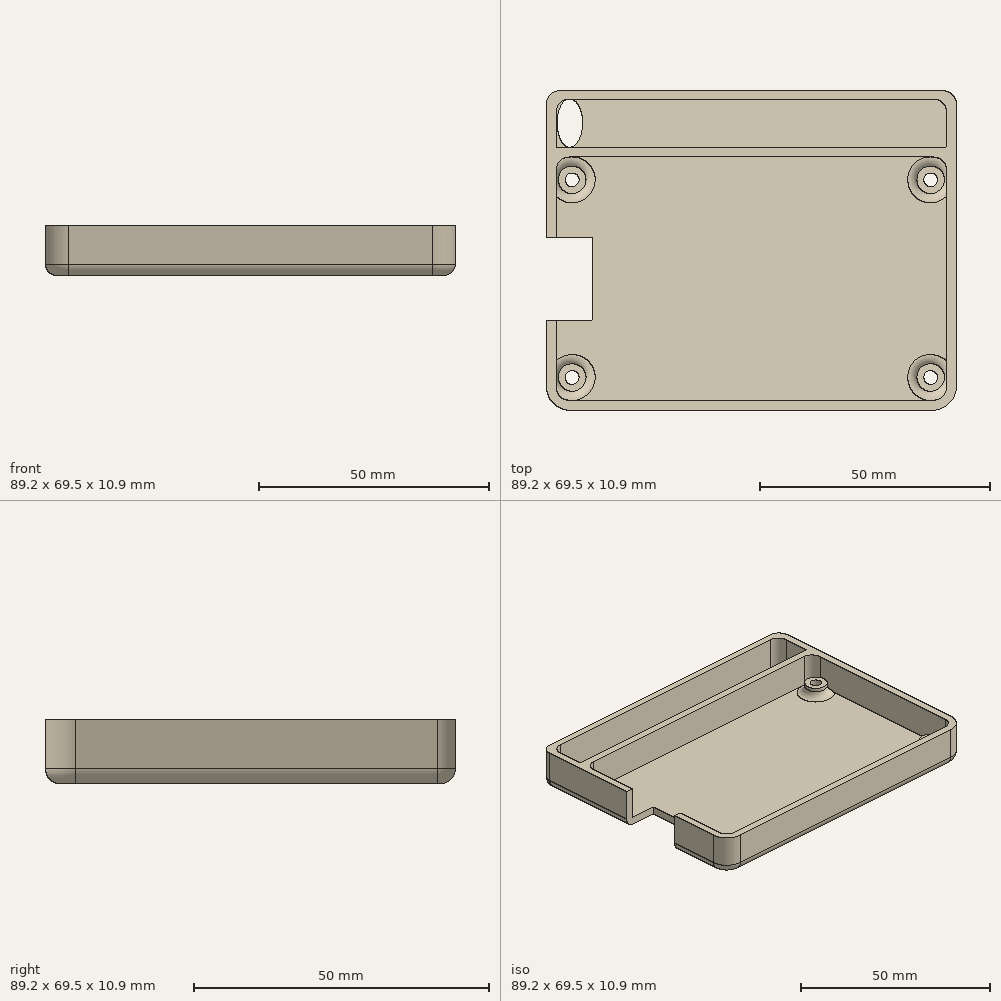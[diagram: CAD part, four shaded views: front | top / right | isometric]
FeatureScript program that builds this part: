
annotation { "Feature Type Name" : "Feature", "Feature Type Description" : "" }
export const myFeature = defineFeature(function(context is Context, id is Id, definition is map)
    precondition{}
    {
        {
            var Q0;
            Q0=qCreatedBy(makeId("Top.planeOp"),FACE);
            var sketch = newSketch(context, id + "F0", { "sketchPlane" : qUnion([Q0])});
            skLineSegment(sketch, "E0.bottom", {"start": v(-39.5, 26.5) * mm, "end": v(39.5, 26.5) * mm});
            skLineSegment(sketch, "E0.top", {"start": v(-39.5, -26.5) * mm, "end": v(39.5, -26.5) * mm});
            skLineSegment(sketch, "E0.left", {"start": v(-42.5, 23.5) * mm, "end": v(-42.5, -23.5) * mm});
            skLineSegment(sketch, "E0.right", {"start": v(42.5, 23.5) * mm, "end": v(42.5, -23.5) * mm});
            skPoint(sketch, "E0.middle", {"position": v(0, 0) * mm});
            skLineSegment(sketch, "E1.bottom", {"start": v(-39, 21.5) * mm, "end": v(39, 21.5) * mm, "construction": true});
            skLineSegment(sketch, "E1.top", {"start": v(-39, -21.5) * mm, "end": v(39, -21.5) * mm, "construction": true});
            skLineSegment(sketch, "E1.left", {"start": v(-39, 21.5) * mm, "end": v(-39, -21.5) * mm, "construction": true});
            skLineSegment(sketch, "E1.right", {"start": v(39, 21.5) * mm, "end": v(39, -21.5) * mm, "construction": true});
            skCircle(sketch, "E2", {"center": v(-39, 21.5) * mm, "radius": 1.5 * mm});
            skCircle(sketch, "E3", {"center": v(39, 21.5) * mm, "radius": 1.5 * mm});
            skCircle(sketch, "E4", {"center": v(39, -21.5) * mm, "radius": 1.5 * mm});
            skCircle(sketch, "E5", {"center": v(-39, -21.5) * mm, "radius": 1.5 * mm});
            skPoint(sketch, "E6.visualSharp", {"position": v(-42.5, 26.5) * mm});
            skArc(sketch, "E6.filletArc", {"start": v(-39.5, 26.5) * mm, "mid": v(-41.62, 25.62) * mm, "end": v(-42.5, 23.5) * mm});
            skPoint(sketch, "E7.visualSharp", {"position": v(42.5, 26.5) * mm});
            skArc(sketch, "E7.filletArc", {"start": v(42.5, 23.5) * mm, "mid": v(41.62, 25.62) * mm, "end": v(39.5, 26.5) * mm});
            skPoint(sketch, "E8.visualSharp", {"position": v(42.5, -26.5) * mm});
            skArc(sketch, "E8.filletArc", {"start": v(39.5, -26.5) * mm, "mid": v(41.62, -25.62) * mm, "end": v(42.5, -23.5) * mm});
            skPoint(sketch, "E9.visualSharp", {"position": v(-42.5, -26.5) * mm});
            skArc(sketch, "E9.filletArc", {"start": v(-42.5, -23.5) * mm, "mid": v(-41.62, -25.62) * mm, "end": v(-39.5, -26.5) * mm});
            skLineSegment(sketch, "E10", {"start": v(0, 0) * mm, "end": v(-34.5, 0) * mm, "construction": true});
            skLineSegment(sketch, "E11", {"start": v(-34.5, 26.5) * mm, "end": v(-34.5, -26.5) * mm});
            skLineSegment(sketch, "E12", {"start": v(0, 0) * mm, "end": v(0, 9.32) * mm, "construction": true});
            skLineSegment(sketch, "E13.MirrorCS", {"start": v(34.5, 26.5) * mm, "end": v(34.5, -26.5) * mm});
            skLineSegment(sketch, "E14.1", {"start": v(-44.6, 23.5) * mm, "end": v(-44.6, -23.5) * mm});
            skLineSegment(sketch, "E14.2", {"start": v(-39.5, 28.6) * mm, "end": v(39.5, 28.6) * mm});
            skArc(sketch, "E14.3", {"start": v(-44.6, -23.5) * mm, "mid": v(-43.1, -27.1) * mm, "end": v(-39.5, -28.6) * mm});
            skLineSegment(sketch, "E14.5", {"start": v(44.6, 23.5) * mm, "end": v(44.6, -23.5) * mm});
            skArc(sketch, "E14.6", {"start": v(39.5, -28.6) * mm, "mid": v(43.1, -27.1) * mm, "end": v(44.6, -23.5) * mm});
            skLineSegment(sketch, "E14.7", {"start": v(-39.5, -28.6) * mm, "end": v(39.5, -28.6) * mm});
            skLineSegment(sketch, "E15", {"start": v(-42.5, 0) * mm, "end": v(-44.6, 0) * mm, "construction": true});
            skLineSegment(sketch, "E16.bottom", {"start": v(-44.6, 9) * mm, "end": v(-42.5, 9) * mm});
            skLineSegment(sketch, "E16.top", {"start": v(-44.6, -9) * mm, "end": v(-42.5, -9) * mm});
            skLineSegment(sketch, "E16.left", {"start": v(-44.6, 9) * mm, "end": v(-44.6, -9) * mm});
            skLineSegment(sketch, "E16.right", {"start": v(-42.5, 9) * mm, "end": v(-42.5, -9) * mm});
            skPoint(sketch, "E16.middle", {"position": v(-43.55, 0) * mm});
            skLineSegment(sketch, "E17", {"start": v(-42.5, 9) * mm, "end": v(-34.5, 9) * mm});
            skLineSegment(sketch, "E18", {"start": v(-42.5, -9) * mm, "end": v(-34.5, -9) * mm});
            skLineSegment(sketch, "E19", {"start": v(0, 28.6) * mm, "end": v(0, 39.1) * mm, "construction": true});
            skLineSegment(sketch, "E20", {"start": v(0, 39.1) * mm, "end": v(-39.5, 39.1) * mm});
            skLineSegment(sketch, "E21", {"start": v(0, 39.1) * mm, "end": v(39.5, 39.1) * mm});
            skLineSegment(sketch, "E22.0", {"start": v(0, 40.9) * mm, "end": v(41.6, 40.9) * mm});
            skLineSegment(sketch, "E22.1", {"start": v(0, 40.9) * mm, "end": v(-41.6, 40.9) * mm});
            skLineSegment(sketch, "E23", {"start": v(-42.5, 23.5) * mm, "end": v(-42.5, 36.1) * mm});
            skLineSegment(sketch, "E24", {"start": v(42.5, 23.5) * mm, "end": v(42.5, 36.1) * mm});
            skPoint(sketch, "E25.visualSharp", {"position": v(42.5, 39.1) * mm});
            skArc(sketch, "E25.filletArc", {"start": v(42.5, 36.1) * mm, "mid": v(41.62, 38.22) * mm, "end": v(39.5, 39.1) * mm});
            skPoint(sketch, "E26.visualSharp", {"position": v(-42.5, 39.1) * mm});
            skArc(sketch, "E26.filletArc", {"start": v(-39.5, 39.1) * mm, "mid": v(-41.62, 38.22) * mm, "end": v(-42.5, 36.1) * mm});
            skPoint(sketch, "E27.start.orphan", {"position": v(-44.6, 39.1) * mm});
            skPoint(sketch, "E28.start.orphan", {"position": v(44.6, 39.1) * mm});
            skLineSegment(sketch, "E29", {"start": v(-44.6, 23.5) * mm, "end": v(-44.6, 37.9) * mm});
            skLineSegment(sketch, "E30", {"start": v(44.6, 23.5) * mm, "end": v(44.6, 37.9) * mm});
            skPoint(sketch, "E31.visualSharp", {"position": v(-44.6, 40.9) * mm});
            skArc(sketch, "E31.filletArc", {"start": v(-41.6, 40.9) * mm, "mid": v(-43.72, 40.02) * mm, "end": v(-44.6, 37.9) * mm});
            skPoint(sketch, "E32.visualSharp", {"position": v(44.6, 40.9) * mm});
            skArc(sketch, "E32.filletArc", {"start": v(44.6, 37.9) * mm, "mid": v(43.72, 40.02) * mm, "end": v(41.6, 40.9) * mm});
            skLineSegment(sketch, "E33", {"start": v(-39.5, 28.6) * mm, "end": v(-42.5, 28.6) * mm});
            skLineSegment(sketch, "E34", {"start": v(39.5, 28.6) * mm, "end": v(42.5, 28.6) * mm});
            skEllipse(sketch, "E35", {"center": v(-39.5, 33.85) * mm, "majorRadius": 5.25 * mm, "minorRadius": 2.78 * mm, "majorAxis": v(0, 1)});
            skPoint(sketch, "E35.centerSnap0", {"position": v(0, 33.85) * mm});
            skCircle(sketch, "E36", {"center": v(-39, 21.5) * mm, "radius": 3 * mm});
            skCircle(sketch, "E37", {"center": v(39, 21.5) * mm, "radius": 3 * mm});
            skCircle(sketch, "E38", {"center": v(39, -21.5) * mm, "radius": 3 * mm});
            skCircle(sketch, "E39", {"center": v(-39, -21.5) * mm, "radius": 3 * mm});
            skSolve(sketch);
        }
        {
            var Q0;
            {var subQ13=sQuery(id+"F0.wireOp",EDGE,"E0.right");Q0=makeQuery(id+"F0.imprint","IMPRINT",FACE,{"disambiguationData":[TD([[makeQuery(id+"F0.imprint","IMPRINT",EDGE,{"derivedFrom":subQ13}),1.0]])]});}
            var Q1;
            Q1=makeQuery(id+"F0.imprint","IMPRINT",FACE,{"disambiguationData":[TD([[makeQuery(id+"F0.imprint","IMPRINT",EDGE,{"derivedFrom":sQuery(id+"F0.wireOp",EDGE,"E2")}),-1.0]])]});
            var Q2;
            Q2=makeQuery(id+"F0.imprint","IMPRINT",FACE,{"disambiguationData":[TD([[makeQuery(id+"F0.imprint","IMPRINT",EDGE,{"derivedFrom":sQuery(id+"F0.wireOp",EDGE,"E5")}),-1.0]])]});
            var Q3;
            {var subQ5=sQuery(id+"F0.wireOp",EDGE,"E13.MirrorCS");Q3=makeQuery(id+"F0.imprint","IMPRINT",FACE,{"disambiguationData":[TD([[makeQuery(id+"F0.imprint","IMPRINT",EDGE,{"derivedFrom":subQ5}),-1.0]])]});}
            var Q4;
            Q4=makeQuery(id+"F0.imprint","IMPRINT",FACE,{"disambiguationData":[TD([[makeQuery(id+"F0.imprint","IMPRINT",EDGE,{"derivedFrom":sQuery(id+"F0.wireOp",EDGE,"E0.right")}),-1.0]])]});
            var Q5;
            {var subQ0=sQuery(id+"F0.wireOp",EDGE,"E6.filletArc");Q5=makeQuery(id+"F0.imprint","IMPRINT",FACE,{"disambiguationData":[TD([[makeQuery(id+"F0.imprint","IMPRINT",EDGE,{"derivedFrom":subQ0}),-1.0]])]});}
            var Q6;
            {var subQ5=sQuery(id+"F0.wireOp",EDGE,"E14.2");Q6=makeQuery(id+"F0.imprint","IMPRINT",FACE,{"disambiguationData":[TD([[makeQuery(id+"F0.imprint","IMPRINT",EDGE,{"derivedFrom":subQ5}),1.0]])]});}
            var Q7;
            {var subQ0=sQuery(id+"F0.wireOp",EDGE,"E6.filletArc");Q7=makeQuery(id+"F0.imprint","IMPRINT",FACE,{"disambiguationData":[TD([[makeQuery(id+"F0.imprint","IMPRINT",EDGE,{"derivedFrom":subQ0}),-1.0]])]});}
            var Q8;
            {var subQ2=sQuery(id+"F0.wireOp",EDGE,"E26.filletArc");Q8=makeQuery(id+"F0.imprint","IMPRINT",FACE,{"disambiguationData":[TD([[makeQuery(id+"F0.imprint","IMPRINT",EDGE,{"derivedFrom":subQ2}),1.0]])]});}
            var Q9;
            {var subQ4=sQuery(id+"F0.wireOp",EDGE,"E6.filletArc");Q9=makeQuery(id+"F0.imprint","IMPRINT",FACE,{"disambiguationData":[TD([[makeQuery(id+"F0.imprint","IMPRINT",EDGE,{"derivedFrom":subQ4}),1.0]])]});}
            var Q10;
            {var subQ4=sQuery(id+"F0.wireOp",EDGE,"E9.filletArc");Q10=makeQuery(id+"F0.imprint","IMPRINT",FACE,{"disambiguationData":[TD([[makeQuery(id+"F0.imprint","IMPRINT",EDGE,{"derivedFrom":subQ4}),1.0]])]});}
            var Q11;
            Q11=makeQuery(id+"F0.imprint","IMPRINT",FACE,{"disambiguationData":[TD([[makeQuery(id+"F0.imprint","IMPRINT",EDGE,{"derivedFrom":sQuery(id+"F0.wireOp",EDGE,"E3")}),-1.0]])]});
            var Q12;
            Q12=makeQuery(id+"F0.imprint","IMPRINT",FACE,{"disambiguationData":[TD([[makeQuery(id+"F0.imprint","IMPRINT",EDGE,{"derivedFrom":sQuery(id+"F0.wireOp",EDGE,"E4")}),-1.0]])]});
            extrude(context, id + "F1", {"entities" : qUnion([Q0, Q1, Q2, Q3, Q4, Q5, Q6, Q7, Q8, Q9, Q10, Q11, Q12]), "depth" : 2.1 * mm, "offsetDistance" : 25 * mm});
        }
        {
            var Q0;
            {var subQ13=sQuery(id+"F0.wireOp",EDGE,"E0.right");Q0=makeQuery(id+"F0.imprint","IMPRINT",FACE,{"disambiguationData":[TD([[makeQuery(id+"F0.imprint","IMPRINT",EDGE,{"derivedFrom":subQ13}),1.0]])]});}
            var Q1;
            {var subQ0=sQuery(id+"F0.wireOp",EDGE,"E6.filletArc");Q1=makeQuery(id+"F0.imprint","IMPRINT",FACE,{"disambiguationData":[TD([[makeQuery(id+"F0.imprint","IMPRINT",EDGE,{"derivedFrom":subQ0}),-1.0]])]});}
            extrude(context, id + "F2", {"entities" : qUnion([Q0, Q1]), "operationType" : NewBodyOperationType.ADD, "depth" : (5.1 + 5.8) * mm, "offsetDistance" : 25 * mm});
        }
        {
            var Q0;
            Q0=makeQuery(id+"F1.opExtrude","CAP_EDGE",EDGE,{"disambiguationData":[OSD([sQuery(id+"F0.wireOp",EDGE,"E14.5"),sQuery(id+"F0.wireOp",EDGE,"E30")])],"isStart":true});
            fillet(context, id + "F3", {"entities" : qUnion([Q0]), "radius" : 2.5 * mm, "tangentPropagation" : true, "allowEdgeOverflow" : false});
        }
        {
            var Q0;
            Q0=makeQuery(id+"F0.imprint","IMPRINT",FACE,{"disambiguationData":[TD([[makeQuery(id+"F0.imprint","IMPRINT",EDGE,{"derivedFrom":sQuery(id+"F0.wireOp",EDGE,"E2")}),-1.0]])]});
            var Q1;
            Q1=makeQuery(id+"F0.imprint","IMPRINT",FACE,{"disambiguationData":[TD([[makeQuery(id+"F0.imprint","IMPRINT",EDGE,{"derivedFrom":sQuery(id+"F0.wireOp",EDGE,"E3")}),-1.0]])]});
            var Q2;
            Q2=makeQuery(id+"F0.imprint","IMPRINT",FACE,{"disambiguationData":[TD([[makeQuery(id+"F0.imprint","IMPRINT",EDGE,{"derivedFrom":sQuery(id+"F0.wireOp",EDGE,"E4")}),-1.0]])]});
            var Q3;
            Q3=makeQuery(id+"F0.imprint","IMPRINT",FACE,{"disambiguationData":[TD([[makeQuery(id+"F0.imprint","IMPRINT",EDGE,{"derivedFrom":sQuery(id+"F0.wireOp",EDGE,"E5")}),-1.0]])]});
            extrude(context, id + "F4", {"entities" : qUnion([Q0, Q1, Q2, Q3]), "operationType" : NewBodyOperationType.ADD, "depth" : 5.1 * mm, "offsetDistance" : 25 * mm});
        }
        {
            var Q0;
            {var subQ2=sQuery(id+"F0.wireOp",EDGE,"E18");var subQ3=sQuery(id+"F0.wireOp",EDGE,"E16.top");var subQ4=sQuery(id+"F0.wireOp",EDGE,"E17");var subQ5=sQuery(id+"F0.wireOp",EDGE,"E16.bottom");var subQ6=sQuery(id+"F0.wireOp",EDGE,"E11");var subQ7=sQuery(id+"F0.wireOp",EDGE,"E2");var subQ8=sQuery(id+"F0.wireOp",EDGE,"E5");var subQ10=sQuery(id+"F0.wireOp",EDGE,"E3");var subQ11=sQuery(id+"F0.wireOp",EDGE,"E4");Q0=makeQuery(id+"F4.boolean.opBoolean","INTERSECT",EDGE,{"derivedFrom":[makeQuery(id+"F2.boolean.opBoolean","SPLIT",FACE,{"disambiguationData":[TD([makeQuery(id+"F1.opExtrude","SWEPT_FACE",FACE,{"disambiguationData":[OSD([subQ7])]})])],"derivedFrom":makeQuery(id+"F1.opExtrude","CAP_FACE",FACE,{"disambiguationData":[OSD([subQ7,subQ10,subQ11,subQ8,subQ6,sQuery(id+"F0.wireOp",EDGE,"E14.1"),sQuery(id+"F0.wireOp",EDGE,"E14.3"),sQuery(id+"F0.wireOp",EDGE,"E14.5"),sQuery(id+"F0.wireOp",EDGE,"E14.6"),sQuery(id+"F0.wireOp",EDGE,"E14.7"),subQ5,subQ3,subQ4,subQ2,sQuery(id+"F0.wireOp",EDGE,"E22.0"),sQuery(id+"F0.wireOp",EDGE,"E22.1"),sQuery(id+"F0.wireOp",EDGE,"E29"),sQuery(id+"F0.wireOp",EDGE,"E30"),sQuery(id+"F0.wireOp",EDGE,"E31.filletArc"),sQuery(id+"F0.wireOp",EDGE,"E32.filletArc"),sQuery(id+"F0.wireOp",EDGE,"E35")])],"isStart":false})}),makeQuery(id+"F4.opExtrude","SWEPT_FACE",FACE,{"disambiguationData":[OSD([sQuery(id+"F0.wireOp",EDGE,"E36")])]})]});}
            var Q1;
            {var subQ2=sQuery(id+"F0.wireOp",EDGE,"E18");var subQ3=sQuery(id+"F0.wireOp",EDGE,"E16.top");var subQ4=sQuery(id+"F0.wireOp",EDGE,"E17");var subQ5=sQuery(id+"F0.wireOp",EDGE,"E16.bottom");var subQ6=sQuery(id+"F0.wireOp",EDGE,"E11");var subQ7=sQuery(id+"F0.wireOp",EDGE,"E2");var subQ8=sQuery(id+"F0.wireOp",EDGE,"E5");var subQ10=sQuery(id+"F0.wireOp",EDGE,"E3");var subQ11=sQuery(id+"F0.wireOp",EDGE,"E4");Q1=makeQuery(id+"F4.boolean.opBoolean","INTERSECT",EDGE,{"derivedFrom":[makeQuery(id+"F2.boolean.opBoolean","SPLIT",FACE,{"disambiguationData":[TD([makeQuery(id+"F1.opExtrude","SWEPT_FACE",FACE,{"disambiguationData":[OSD([subQ7])]})])],"derivedFrom":makeQuery(id+"F1.opExtrude","CAP_FACE",FACE,{"disambiguationData":[OSD([subQ7,subQ10,subQ11,subQ8,subQ6,sQuery(id+"F0.wireOp",EDGE,"E14.1"),sQuery(id+"F0.wireOp",EDGE,"E14.3"),sQuery(id+"F0.wireOp",EDGE,"E14.5"),sQuery(id+"F0.wireOp",EDGE,"E14.6"),sQuery(id+"F0.wireOp",EDGE,"E14.7"),subQ5,subQ3,subQ4,subQ2,sQuery(id+"F0.wireOp",EDGE,"E22.0"),sQuery(id+"F0.wireOp",EDGE,"E22.1"),sQuery(id+"F0.wireOp",EDGE,"E29"),sQuery(id+"F0.wireOp",EDGE,"E30"),sQuery(id+"F0.wireOp",EDGE,"E31.filletArc"),sQuery(id+"F0.wireOp",EDGE,"E32.filletArc"),sQuery(id+"F0.wireOp",EDGE,"E35")])],"isStart":false})}),makeQuery(id+"F4.opExtrude","SWEPT_FACE",FACE,{"disambiguationData":[OSD([sQuery(id+"F0.wireOp",EDGE,"E37")])]})]});}
            var Q2;
            {var subQ2=sQuery(id+"F0.wireOp",EDGE,"E18");var subQ3=sQuery(id+"F0.wireOp",EDGE,"E16.top");var subQ4=sQuery(id+"F0.wireOp",EDGE,"E17");var subQ5=sQuery(id+"F0.wireOp",EDGE,"E16.bottom");var subQ6=sQuery(id+"F0.wireOp",EDGE,"E11");var subQ7=sQuery(id+"F0.wireOp",EDGE,"E2");var subQ8=sQuery(id+"F0.wireOp",EDGE,"E5");var subQ10=sQuery(id+"F0.wireOp",EDGE,"E3");var subQ11=sQuery(id+"F0.wireOp",EDGE,"E4");Q2=makeQuery(id+"F4.boolean.opBoolean","INTERSECT",EDGE,{"derivedFrom":[makeQuery(id+"F2.boolean.opBoolean","SPLIT",FACE,{"disambiguationData":[TD([makeQuery(id+"F1.opExtrude","SWEPT_FACE",FACE,{"disambiguationData":[OSD([subQ7])]})])],"derivedFrom":makeQuery(id+"F1.opExtrude","CAP_FACE",FACE,{"disambiguationData":[OSD([subQ7,subQ10,subQ11,subQ8,subQ6,sQuery(id+"F0.wireOp",EDGE,"E14.1"),sQuery(id+"F0.wireOp",EDGE,"E14.3"),sQuery(id+"F0.wireOp",EDGE,"E14.5"),sQuery(id+"F0.wireOp",EDGE,"E14.6"),sQuery(id+"F0.wireOp",EDGE,"E14.7"),subQ5,subQ3,subQ4,subQ2,sQuery(id+"F0.wireOp",EDGE,"E22.0"),sQuery(id+"F0.wireOp",EDGE,"E22.1"),sQuery(id+"F0.wireOp",EDGE,"E29"),sQuery(id+"F0.wireOp",EDGE,"E30"),sQuery(id+"F0.wireOp",EDGE,"E31.filletArc"),sQuery(id+"F0.wireOp",EDGE,"E32.filletArc"),sQuery(id+"F0.wireOp",EDGE,"E35")])],"isStart":false})}),makeQuery(id+"F4.opExtrude","SWEPT_FACE",FACE,{"disambiguationData":[OSD([sQuery(id+"F0.wireOp",EDGE,"E38")])]})]});}
            var Q3;
            {var subQ2=sQuery(id+"F0.wireOp",EDGE,"E18");var subQ3=sQuery(id+"F0.wireOp",EDGE,"E16.top");var subQ4=sQuery(id+"F0.wireOp",EDGE,"E17");var subQ5=sQuery(id+"F0.wireOp",EDGE,"E16.bottom");var subQ6=sQuery(id+"F0.wireOp",EDGE,"E11");var subQ7=sQuery(id+"F0.wireOp",EDGE,"E2");var subQ8=sQuery(id+"F0.wireOp",EDGE,"E5");var subQ10=sQuery(id+"F0.wireOp",EDGE,"E3");var subQ11=sQuery(id+"F0.wireOp",EDGE,"E4");Q3=makeQuery(id+"F4.boolean.opBoolean","INTERSECT",EDGE,{"derivedFrom":[makeQuery(id+"F2.boolean.opBoolean","SPLIT",FACE,{"disambiguationData":[TD([makeQuery(id+"F1.opExtrude","SWEPT_FACE",FACE,{"disambiguationData":[OSD([subQ7])]})])],"derivedFrom":makeQuery(id+"F1.opExtrude","CAP_FACE",FACE,{"disambiguationData":[OSD([subQ7,subQ10,subQ11,subQ8,subQ6,sQuery(id+"F0.wireOp",EDGE,"E14.1"),sQuery(id+"F0.wireOp",EDGE,"E14.3"),sQuery(id+"F0.wireOp",EDGE,"E14.5"),sQuery(id+"F0.wireOp",EDGE,"E14.6"),sQuery(id+"F0.wireOp",EDGE,"E14.7"),subQ5,subQ3,subQ4,subQ2,sQuery(id+"F0.wireOp",EDGE,"E22.0"),sQuery(id+"F0.wireOp",EDGE,"E22.1"),sQuery(id+"F0.wireOp",EDGE,"E29"),sQuery(id+"F0.wireOp",EDGE,"E30"),sQuery(id+"F0.wireOp",EDGE,"E31.filletArc"),sQuery(id+"F0.wireOp",EDGE,"E32.filletArc"),sQuery(id+"F0.wireOp",EDGE,"E35")])],"isStart":false})}),makeQuery(id+"F4.opExtrude","SWEPT_FACE",FACE,{"disambiguationData":[OSD([sQuery(id+"F0.wireOp",EDGE,"E39")])]})]});}
            fillet(context, id + "F5", {"entities" : qUnion([Q0, Q1, Q2, Q3]), "radius" : 2 * mm, "tangentPropagation" : true, "allowEdgeOverflow" : false});
        }
    });
